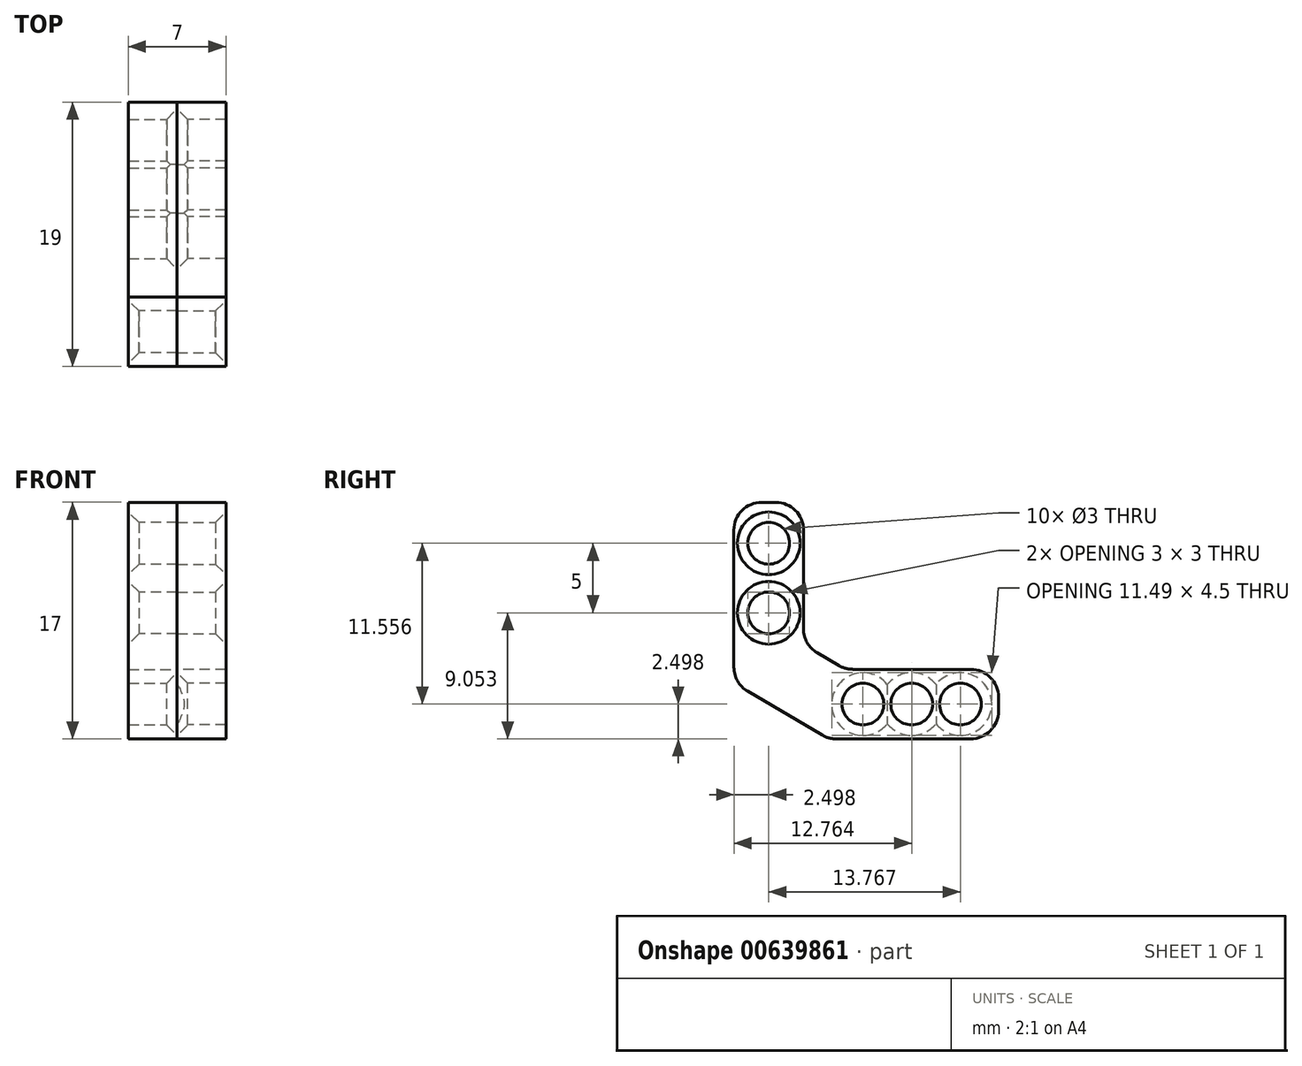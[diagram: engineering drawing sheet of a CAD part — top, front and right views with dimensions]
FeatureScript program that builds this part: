
annotation { "Feature Type Name" : "Feature", "Feature Type Description" : "" }
export const myFeature = defineFeature(function(context is Context, id is Id, definition is map)
    precondition{}
    {
        {
            var Q0;
            Q0=qCreatedBy(makeId("Right.planeOp"),FACE);
            var sketch = newSketch(context, id + "F0", { "sketchPlane" : qUnion([Q0])});
            skLineSegment(sketch, "E0", {"start": v(7.52, 5) * mm, "end": v(7.52, 14.85) * mm});
            skLineSegment(sketch, "E1", {"start": v(9.52, 16.85) * mm, "end": v(10.52, 16.85) * mm});
            skLineSegment(sketch, "E2", {"start": v(12.52, 14.85) * mm, "end": v(12.52, 7.76) * mm});
            skLineSegment(sketch, "E3", {"start": v(10.02, 16.85) * mm, "end": v(10.02, 14.71) * mm});
            skLineSegment(sketch, "E4", {"start": v(14.86, -0.15) * mm, "end": v(24.52, -0.15) * mm});
            skLineSegment(sketch, "E5", {"start": v(26.52, 1.85) * mm, "end": v(26.52, 2.85) * mm});
            skLineSegment(sketch, "E6", {"start": v(24.52, 4.85) * mm, "end": v(16.06, 4.85) * mm});
            skLineSegment(sketch, "E7", {"start": v(15.05, 5.12) * mm, "end": v(13.5, 6.03) * mm});
            skLineSegment(sketch, "E8", {"start": v(8.5, 3.27) * mm, "end": v(13.84, 0.12) * mm});
            skLineSegment(sketch, "E9", {"start": v(26.52, 2.35) * mm, "end": v(12.63, 2.35) * mm});
            skPoint(sketch, "E10", {"position": v(23.78, 2.35) * mm});
            skPoint(sketch, "E11", {"position": v(20.28, 2.35) * mm});
            skPoint(sketch, "E12", {"position": v(16.78, 2.35) * mm});
            skPoint(sketch, "E13", {"position": v(10.02, 13.9) * mm});
            skPoint(sketch, "E14", {"position": v(10.02, 8.9) * mm});
            skPoint(sketch, "E15.visualSharp", {"position": v(12.52, 6.61) * mm});
            skArc(sketch, "E15.filletArc", {"start": v(12.52, 7.76) * mm, "mid": v(12.78, 6.76) * mm, "end": v(13.5, 6.03) * mm});
            skPoint(sketch, "E16.visualSharp", {"position": v(15.52, 4.85) * mm});
            skArc(sketch, "E16.filletArc", {"start": v(15.05, 5.12) * mm, "mid": v(15.54, 4.92) * mm, "end": v(16.06, 4.85) * mm});
            skPoint(sketch, "E17.visualSharp", {"position": v(7.52, 3.85) * mm});
            skArc(sketch, "E17.filletArc", {"start": v(7.52, 5) * mm, "mid": v(7.78, 4) * mm, "end": v(8.5, 3.27) * mm});
            skPoint(sketch, "E18.visualSharp", {"position": v(14.31, -0.15) * mm});
            skArc(sketch, "E18.filletArc", {"start": v(13.84, 0.12) * mm, "mid": v(14.33, -0.08) * mm, "end": v(14.86, -0.15) * mm});
            skPoint(sketch, "E19.visualSharp", {"position": v(26.52, 4.85) * mm});
            skArc(sketch, "E19.filletArc", {"start": v(26.52, 2.85) * mm, "mid": v(25.93, 4.26) * mm, "end": v(24.52, 4.85) * mm});
            skPoint(sketch, "E20.visualSharp", {"position": v(26.52, -0.15) * mm});
            skArc(sketch, "E20.filletArc", {"start": v(24.52, -0.15) * mm, "mid": v(25.93, 0.43) * mm, "end": v(26.52, 1.85) * mm});
            skPoint(sketch, "E21.visualSharp", {"position": v(12.52, 16.85) * mm});
            skArc(sketch, "E21.filletArc", {"start": v(12.52, 14.85) * mm, "mid": v(11.93, 16.26) * mm, "end": v(10.52, 16.85) * mm});
            skPoint(sketch, "E22.visualSharp", {"position": v(7.52, 16.85) * mm});
            skArc(sketch, "E22.filletArc", {"start": v(9.52, 16.85) * mm, "mid": v(8.1, 16.26) * mm, "end": v(7.52, 14.85) * mm});
            skSolve(sketch);
        }
        {
            var Q0;
            Q0 = qSketchRegion(id + "F0", true);
            extrude(context, id + "F1", {"entities" : qUnion([Q0]), "oppositeDirection" : true, "depth" : 3.5 * mm, "offsetDistance" : 25 * mm});
        }
        {
            var Q0;
            Q0=sQuery(id+"F0.wireOp",VERTEX,"E10");
            var Q1;
            Q1=sQuery(id+"F0.wireOp",VERTEX,"E11");
            var Q2;
            Q2=sQuery(id+"F0.wireOp",VERTEX,"E12");
            var Q3;
            Q3=makeQuery(id+"F1.opExtrude","SWEPT_BODY",BODY,{"disambiguationData":[OSD([sQuery(id+"F0.wireOp",EDGE,"E0"),sQuery(id+"F0.wireOp",EDGE,"E1"),sQuery(id+"F0.wireOp",EDGE,"E2"),sQuery(id+"F0.wireOp",EDGE,"E4"),sQuery(id+"F0.wireOp",EDGE,"E5"),sQuery(id+"F0.wireOp",EDGE,"E6"),sQuery(id+"F0.wireOp",EDGE,"E7"),sQuery(id+"F0.wireOp",EDGE,"E8")])]});
            hole(context, id + "F2", {"style" : HoleStyle.C_SINK, "endStyle" : HoleEndStyle.THROUGH, "holeDiameter" : 3 * mm, "cSinkDiameter" : 4.5 * mm, "cSinkAngle" : 90 * degree, "majorDiameter" : 5 * mm, "isTappedThrough" : true, "tappedDepth" : 12 * mm, "tapClearance" : 3, "locations" : qUnion([Q0, Q1, Q2]), "scope" : qUnion([Q3])});
        }
        {
            var Q0;
            Q0=makeQuery(id+"F1.opExtrude","CAP_FACE",FACE,{"disambiguationData":[OSD([sQuery(id+"F0.wireOp",EDGE,"E0"),sQuery(id+"F0.wireOp",EDGE,"E1"),sQuery(id+"F0.wireOp",EDGE,"E2"),sQuery(id+"F0.wireOp",EDGE,"E4"),sQuery(id+"F0.wireOp",EDGE,"E5"),sQuery(id+"F0.wireOp",EDGE,"E6"),sQuery(id+"F0.wireOp",EDGE,"E7"),sQuery(id+"F0.wireOp",EDGE,"E8")])],"isStart":false});
            var sketch = newSketch(context, id + "F3", { "sketchPlane" : qUnion([Q0])});
            skLineSegment(sketch, "E23", {"start": v(-10.02, 16.85) * mm, "end": v(-10.02, 7.55) * mm});
            skPoint(sketch, "E23.endSnap0", {"position": v(-10.02, 16.85) * mm});
            skPoint(sketch, "E24", {"position": v(-10.02, 13.9) * mm});
            skPoint(sketch, "E25", {"position": v(0, 24.37) * mm});
            skPoint(sketch, "E26", {"position": v(10.9, 30.38) * mm});
            skPoint(sketch, "E27", {"position": v(-10.02, 8.9) * mm});
            skSolve(sketch);
        }
        {
            var Q0;
            Q0=sQuery(id+"F3.wireOp",VERTEX,"E24");
            var Q1;
            Q1=sQuery(id+"F3.wireOp",VERTEX,"E27");
            var Q2;
            Q2=makeQuery(id+"F1.opExtrude","SWEPT_BODY",BODY,{"disambiguationData":[OSD([sQuery(id+"F0.wireOp",EDGE,"E0"),sQuery(id+"F0.wireOp",EDGE,"E1"),sQuery(id+"F0.wireOp",EDGE,"E2"),sQuery(id+"F0.wireOp",EDGE,"E4"),sQuery(id+"F0.wireOp",EDGE,"E5"),sQuery(id+"F0.wireOp",EDGE,"E6"),sQuery(id+"F0.wireOp",EDGE,"E7"),sQuery(id+"F0.wireOp",EDGE,"E8")])]});
            hole(context, id + "F4", {"style" : HoleStyle.C_SINK, "endStyle" : HoleEndStyle.THROUGH, "holeDiameter" : 3 * mm, "cSinkDiameter" : 4.5 * mm, "cSinkAngle" : 90 * degree, "majorDiameter" : 5 * mm, "isTappedThrough" : true, "tappedDepth" : 12 * mm, "tapClearance" : 3, "locations" : qUnion([Q0, Q1]), "scope" : qUnion([Q2])});
        }
        {
            var Q0;
            Q0=makeQuery(id+"F1.opExtrude","SWEPT_BODY",BODY,{"disambiguationData":[OSD([sQuery(id+"F0.wireOp",EDGE,"E0"),sQuery(id+"F0.wireOp",EDGE,"E1"),sQuery(id+"F0.wireOp",EDGE,"E2"),sQuery(id+"F0.wireOp",EDGE,"E4"),sQuery(id+"F0.wireOp",EDGE,"E5"),sQuery(id+"F0.wireOp",EDGE,"E6"),sQuery(id+"F0.wireOp",EDGE,"E7"),sQuery(id+"F0.wireOp",EDGE,"E8"),sQuery(id+"F0.wireOp",EDGE,"E15.filletArc"),sQuery(id+"F0.wireOp",EDGE,"E16.filletArc"),sQuery(id+"F0.wireOp",EDGE,"E17.filletArc"),sQuery(id+"F0.wireOp",EDGE,"E18.filletArc"),sQuery(id+"F0.wireOp",EDGE,"E19.filletArc"),sQuery(id+"F0.wireOp",EDGE,"E20.filletArc"),sQuery(id+"F0.wireOp",EDGE,"E21.filletArc"),sQuery(id+"F0.wireOp",EDGE,"E22.filletArc")])]});
            var Q1;
            Q1=qCreatedBy(makeId("Right.planeOp"),FACE);
            mirror(context, id + "F5", {"entities" : qUnion([Q0]), "mirrorPlane" : qUnion([Q1])});
        }
    });
